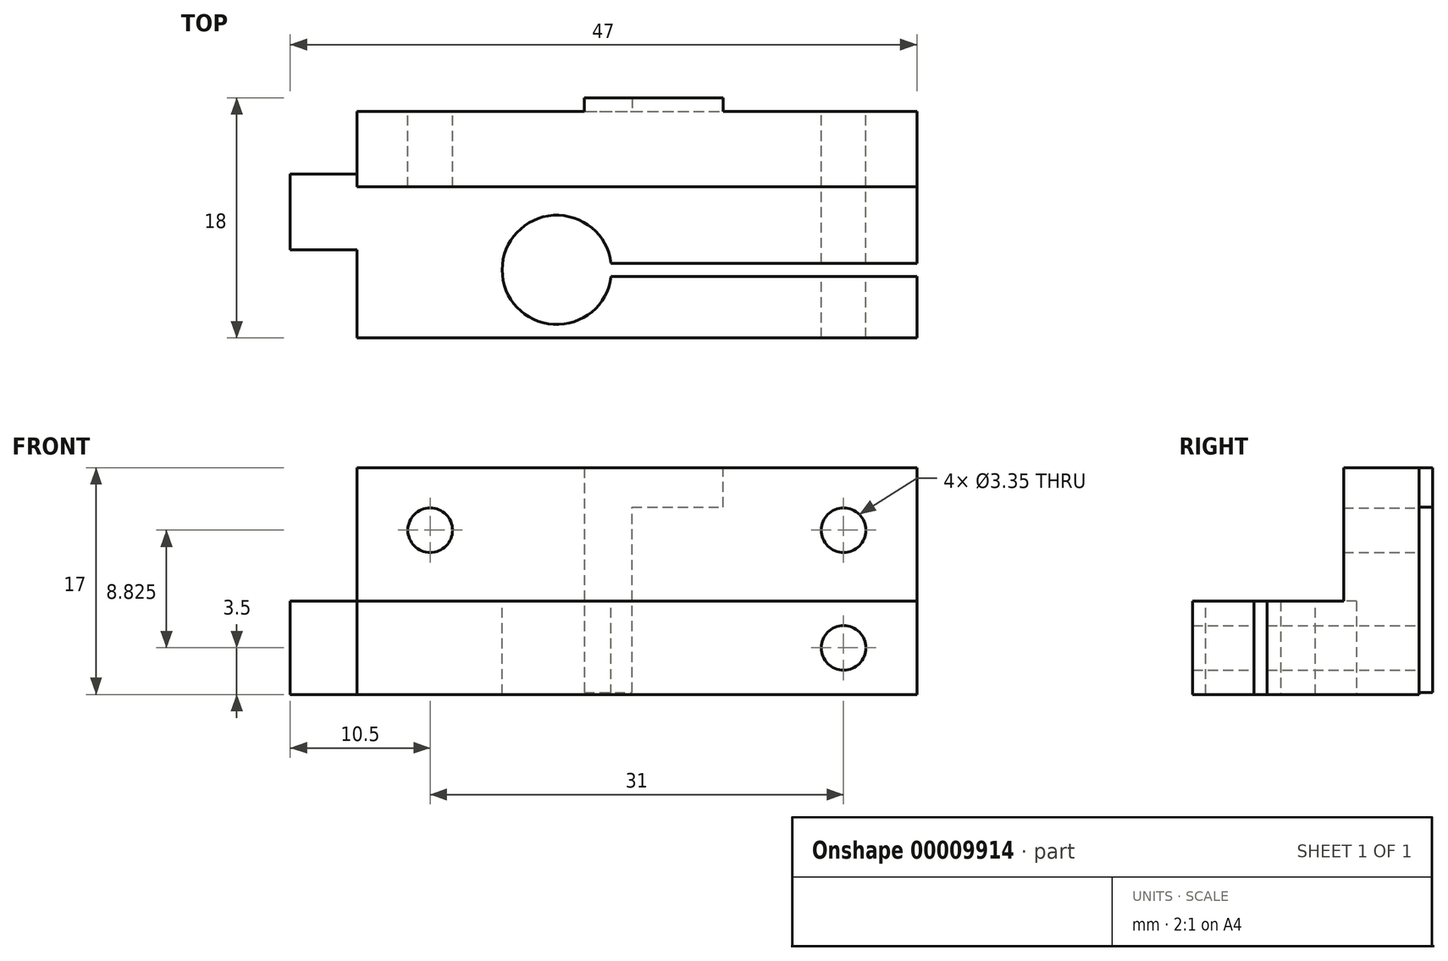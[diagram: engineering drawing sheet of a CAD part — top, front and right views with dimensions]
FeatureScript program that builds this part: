
annotation { "Feature Type Name" : "Feature", "Feature Type Description" : "" }
export const myFeature = defineFeature(function(context is Context, id is Id, definition is map)
    precondition{}
    {
        {
            var Q0;
            Q0=qCreatedBy(makeId("Top.planeOp"),FACE);
            var sketch = newSketch(context, id + "F0", { "sketchPlane" : qUnion([Q0])});
            skLineSegment(sketch, "E0.bottom", {"start": v(0, 0) * mm, "end": v(42, 0) * mm});
            skLineSegment(sketch, "E0.top", {"start": v(0, 17) * mm, "end": v(42, 17) * mm});
            skLineSegment(sketch, "E0.left", {"start": v(0, 0) * mm, "end": v(0, 17) * mm});
            skLineSegment(sketch, "E0.right", {"start": v(42, 0) * mm, "end": v(42, 17) * mm});
            skSolve(sketch);
        }
        {
            var Q0;
            Q0=qSketchRegion(id+"F0",true);
            extrude(context, id + "F1", {"entities" : qUnion([Q0]), "depth" : 7 * mm});
        }
        {
            var Q0;
            Q0=makeQuery(id+"F1.opExtrude","CAP_FACE",FACE,{"disambiguationData":[OSD([sQuery(id+"F0.wireOp",EDGE,"E0.bottom"),sQuery(id+"F0.wireOp",EDGE,"E0.top"),sQuery(id+"F0.wireOp",EDGE,"E0.left"),sQuery(id+"F0.wireOp",EDGE,"E0.right")])],"isStart":false});
            var sketch = newSketch(context, id + "F2", { "sketchPlane" : qUnion([Q0])});
            skCircle(sketch, "E1", {"center": v(15, 5.1) * mm, "radius": 4.1 * mm});
            skLineSegment(sketch, "E2", {"start": v(15, 5.1) * mm, "end": v(42, 5.1) * mm});
            skLineSegment(sketch, "E3", {"start": v(42, 5.1) * mm, "end": v(42, 4.6) * mm});
            skLineSegment(sketch, "E4", {"start": v(42, 4.6) * mm, "end": v(19.07, 4.6) * mm});
            skLineSegment(sketch, "E5", {"start": v(42, 5.1) * mm, "end": v(42, 5.6) * mm});
            skLineSegment(sketch, "E6", {"start": v(42, 5.6) * mm, "end": v(19.07, 5.6) * mm});
            skSolve(sketch);
        }
        {
            var Q0;
            Q0=makeQuery(id+"F1.opExtrude","SWEPT_FACE",FACE,{"disambiguationData":[OSD([sQuery(id+"F0.wireOp",EDGE,"E0.top")])]});
            var sketch = newSketch(context, id + "F3", { "sketchPlane" : qUnion([Q0])});
            skCircle(sketch, "E7", {"center": v(-36.5, 3.5) * mm, "radius": 1.68 * mm});
            skLineSegment(sketch, "E8", {"start": v(-36.5, 3.5) * mm, "end": v(-42, 3.5) * mm});
            skSolve(sketch);
        }
        {
            var Q0;
            Q0=qSketchRegion(id+"F3",true);
            extrude(context, id + "F4", {"entities" : qUnion([Q0]), "operationType" : NewBodyOperationType.REMOVE, "oppositeDirection" : true, "depth" : 25 * mm});
        }
        {
            var Q0;
            Q0=makeQuery(id+"F1.opExtrude","CAP_FACE",FACE,{"disambiguationData":[OSD([sQuery(id+"F0.wireOp",EDGE,"E0.bottom"),sQuery(id+"F0.wireOp",EDGE,"E0.top"),sQuery(id+"F0.wireOp",EDGE,"E0.left"),sQuery(id+"F0.wireOp",EDGE,"E0.right")])],"isStart":false});
            var sketch = newSketch(context, id + "F5", { "sketchPlane" : qUnion([Q0])});
            skLineSegment(sketch, "E9.bottom", {"start": v(0, 17) * mm, "end": v(42, 17) * mm});
            skLineSegment(sketch, "E9.top", {"start": v(0, 11.33) * mm, "end": v(42, 11.33) * mm});
            skLineSegment(sketch, "E9.left", {"start": v(0, 17) * mm, "end": v(0, 11.33) * mm});
            skLineSegment(sketch, "E9.right", {"start": v(42, 17) * mm, "end": v(42, 11.33) * mm});
            skSolve(sketch);
        }
        {
            var Q0;
            Q0=makeQuery(id+"F5.imprint","IMPRINT",FACE,{"disambiguationData":[TD([[makeQuery(id+"F5.imprint","IMPRINT",EDGE,{"derivedFrom":sQuery(id+"F5.wireOp",EDGE,"E9.bottom")}),-1.0]])]});
            extrude(context, id + "F6", {"entities" : qUnion([Q0]), "operationType" : NewBodyOperationType.ADD, "depth" : 10 * mm});
        }
        {
            var Q0;
            Q0=makeQuery(id+"F6.boolean.opBoolean","MERGE",FACE,{"derivedFrom":[makeQuery(id+"F1.opExtrude","SWEPT_FACE",FACE,{"disambiguationData":[OSD([sQuery(id+"F0.wireOp",EDGE,"E0.top")])]}),makeQuery(id+"F6.opExtrude","SWEPT_FACE",FACE,{"disambiguationData":[OSD([sQuery(id+"FFFDCbTcivKPk1C_1.wireOp",EDGE,"d29ae964-e38a-46b3-8ff4-cadffaec6662.bottom")])]})]});
            var sketch = newSketch(context, id + "F7", { "sketchPlane" : qUnion([Q0])});
            skPoint(sketch, "E10", {"position": v(-36.5, 3.5) * mm});
            skCircle(sketch, "E11", {"center": v(-36.5, 12.33) * mm, "radius": 1.68 * mm});
            skCircle(sketch, "E12", {"center": v(-5.5, 12.33) * mm, "radius": 1.68 * mm});
            skSolve(sketch);
        }
        {
            var Q0;
            Q0 = qSketchRegion(id + "F7", true);
            extrude(context, id + "F8", {"entities" : qUnion([Q0]), "operationType" : NewBodyOperationType.REMOVE, "oppositeDirection" : true, "depth" : 25 * mm});
        }
        {
            var Q0;
            Q0 = qSketchRegion(id + "F2", true);
            extrude(context, id + "F9", {"entities" : qUnion([Q0]), "operationType" : NewBodyOperationType.REMOVE, "oppositeDirection" : true, "depth" : 25 * mm});
        }
        {
            var Q0;
            Q0=makeQuery(id+"F6.boolean.opBoolean","MERGE",FACE,{"derivedFrom":[makeQuery(id+"F1.opExtrude","SWEPT_FACE",FACE,{"disambiguationData":[OSD([sQuery(id+"F0.wireOp",EDGE,"E0.top")])]}),makeQuery(id+"F6.opExtrude","SWEPT_FACE",FACE,{"disambiguationData":[OSD([sQuery(id+"F5.wireOp",EDGE,"E9.bottom")])]})]});
            var sketch = newSketch(context, id + "F10", { "sketchPlane" : qUnion([Q0])});
            skText(sketch, "E13", { "text": "L", "fontName": "OpenSans-Bold.ttf"});
            const initialGuessF10  = {"E13": [-0.01494, 0.017, -1, 0, 0.017]};
            skSetInitialGuess(sketch, initialGuessF10);
            skSolve(sketch);
        }
        {
            var Q0;
            Q0 = qSketchRegion(id + "F10", true);
            extrude(context, id + "F11", {"entities" : qUnion([Q0]), "operationType" : NewBodyOperationType.ADD, "depth" : 1 * mm});
        }
        {
            var Q0;
            Q0=makeQuery(id+"F6.boolean.opBoolean","MERGE",FACE,{"derivedFrom":[makeQuery(id+"F1.opExtrude","SWEPT_FACE",FACE,{"disambiguationData":[OSD([sQuery(id+"F0.wireOp",EDGE,"E0.left")])]}),makeQuery(id+"F6.opExtrude","SWEPT_FACE",FACE,{"disambiguationData":[OSD([sQuery(id+"F5.wireOp",EDGE,"E9.left")])]})]});
            var sketch = newSketch(context, id + "F12", { "sketchPlane" : qUnion([Q0])});
            skLineSegment(sketch, "E14.bottom", {"start": v(-12.3, 7) * mm, "end": v(-6.6, 7) * mm});
            skLineSegment(sketch, "E14.top", {"start": v(-12.3, 0) * mm, "end": v(-6.6, 0) * mm});
            skLineSegment(sketch, "E14.left", {"start": v(-12.3, 7) * mm, "end": v(-12.3, 0) * mm});
            skLineSegment(sketch, "E14.right", {"start": v(-6.6, 7) * mm, "end": v(-6.6, 0) * mm});
            skSolve(sketch);
        }
        {
            var Q0;
            Q0 = qSketchRegion(id + "F12", true);
            extrude(context, id + "F13", {"entities" : qUnion([Q0]), "operationType" : NewBodyOperationType.ADD, "depth" : 5 * mm});
        }
    });
